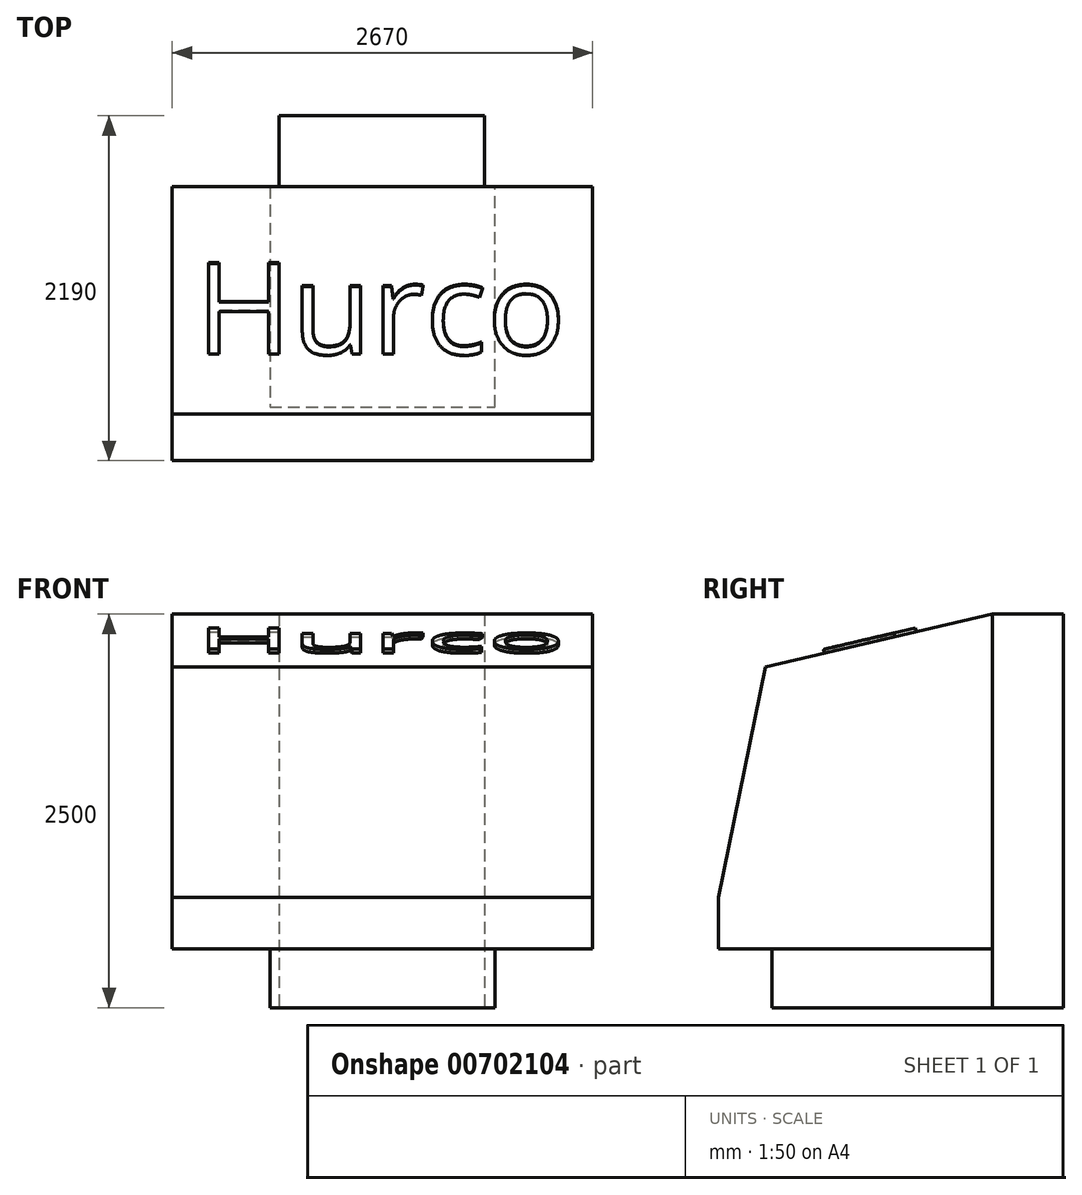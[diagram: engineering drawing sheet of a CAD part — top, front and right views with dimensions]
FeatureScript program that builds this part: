
annotation { "Feature Type Name" : "Feature", "Feature Type Description" : "" }
export const myFeature = defineFeature(function(context is Context, id is Id, definition is map)
    precondition{}
    {
        {
            var Q0;
            Q0=qCreatedBy(makeId("Top.planeOp"),FACE);
            var sketch = newSketch(context, id + "F0", { "sketchPlane" : qUnion([Q0])});
            skLineSegment(sketch, "E0.bottom", {"start": v(0, 0) * mm, "end": v(2670, 0) * mm});
            skLineSegment(sketch, "E0.top", {"start": v(0, 1740) * mm, "end": v(680, 1740) * mm});
            skLineSegment(sketch, "E0.left", {"start": v(0, 0) * mm, "end": v(0, 1740) * mm});
            skLineSegment(sketch, "E0.right", {"start": v(2670, 0) * mm, "end": v(2670, 1740) * mm});
            skLineSegment(sketch, "E1.top", {"start": v(680, 2190) * mm, "end": v(1985, 2190) * mm});
            skLineSegment(sketch, "E1.left", {"start": v(680, 1740) * mm, "end": v(680, 2190) * mm});
            skLineSegment(sketch, "E1.right", {"start": v(1985, 1740) * mm, "end": v(1985, 2190) * mm});
            skLineSegment(sketch, "E2.trimOffspring", {"start": v(1985, 1740) * mm, "end": v(2670, 1740) * mm});
            skSolve(sketch);
        }
        {
            var Q0;
            Q0=makeQuery(id+"F0.imprint","IMPRINT",FACE,{"disambiguationData":[TD([[makeQuery(id+"F0.imprint","IMPRINT",EDGE,{"derivedFrom":sQuery(id+"F0.wireOp",EDGE,"E0.bottom")}),1.0]])]});
            extrude(context, id + "F1", {"entities" : qUnion([Q0]), "depth" : 2500 * mm, "offsetDistance" : 25 * mm});
        }
        {
            var Q0;
            Q0=makeQuery(id+"F1.opExtrude","SWEPT_FACE",FACE,{"disambiguationData":[OSD([sQuery(id+"F0.wireOp",EDGE,"E0.right")])]});
            var sketch = newSketch(context, id + "F2", { "sketchPlane" : qUnion([Q0])});
            skLineSegment(sketch, "E3", {"start": v(0, 700) * mm, "end": v(296.46, 2163.72) * mm});
            skLineSegment(sketch, "E4", {"start": v(296.46, 2163.72) * mm, "end": v(1740, 2500) * mm});
            skLineSegment(sketch, "E5", {"start": v(1740, 2500) * mm, "end": v(0, 2500) * mm});
            skLineSegment(sketch, "E6", {"start": v(0, 2500) * mm, "end": v(0, 700) * mm});
            skSolve(sketch);
        }
        {
            var Q0;
            Q0=makeQuery(id+"F2.imprint","IMPRINT",FACE,{"disambiguationData":[TD([[makeQuery(id+"F2.imprint","IMPRINT",EDGE,{"derivedFrom":sQuery(id+"F2.wireOp",EDGE,"E3")}),1.0]])]});
            extrude(context, id + "F3", {"entities" : qUnion([Q0]), "operationType" : NewBodyOperationType.REMOVE, "endBound" : BoundingType.THROUGH_ALL, "oppositeDirection" : true, "depth" : 25 * mm, "offsetDistance" : 25 * mm});
        }
        {
            var Q0;
            Q0=makeQuery(id+"F3.boolean.opBoolean","COPY",FACE,{"derivedFrom":makeQuery(id+"F3.opExtrude","SWEPT_FACE",FACE,{"disambiguationData":[OSD([sQuery(id+"F2.wireOp",EDGE,"E4")])]})});
            var sketch = newSketch(context, id + "F4", { "sketchPlane" : qUnion([Q0])});
            skText(sketch, "E7", { "text": "Hurco", "fontName": "OpenSans-Regular.ttf"});
            const initialGuessF4  = {"E7": [0.14938, 1.17443, 1, 0, 0.5957]};
            skSetInitialGuess(sketch, initialGuessF4);
            skSolve(sketch);
        }
        {
            var Q0;
            Q0 = qSketchRegion(id + "F4", true);
            extrude(context, id + "F5", {"entities" : qUnion([Q0]), "operationType" : NewBodyOperationType.ADD, "depth" : 25 * mm, "offsetDistance" : 25 * mm});
        }
        {
            var Q0;
            Q0=makeQuery(id+"F1.opExtrude","CAP_FACE",FACE,{"disambiguationData":[OSD([sQuery(id+"F0.wireOp",EDGE,"E0.bottom"),sQuery(id+"F0.wireOp",EDGE,"E0.top"),sQuery(id+"F0.wireOp",EDGE,"E0.left"),sQuery(id+"F0.wireOp",EDGE,"E0.right"),sQuery(id+"F0.wireOp",EDGE,"E1.top"),sQuery(id+"F0.wireOp",EDGE,"E1.left"),sQuery(id+"F0.wireOp",EDGE,"E1.right"),sQuery(id+"F0.wireOp",EDGE,"E2.trimOffspring")])],"isStart":true});
            var sketch = newSketch(context, id + "F6", { "sketchPlane" : qUnion([Q0])});
            skLineSegment(sketch, "E8", {"start": v(0, -1740) * mm, "end": v(620, -1740) * mm});
            skLineSegment(sketch, "E9", {"start": v(620, -1740) * mm, "end": v(620, -340) * mm});
            skLineSegment(sketch, "E10", {"start": v(620, -340) * mm, "end": v(2050, -340) * mm});
            skLineSegment(sketch, "E11", {"start": v(2050, -340) * mm, "end": v(2050, -1740) * mm});
            skLineSegment(sketch, "E12", {"start": v(2050, -1740) * mm, "end": v(2670, -1740) * mm});
            skLineSegment(sketch, "E13", {"start": v(2670, -1740) * mm, "end": v(2670, 0) * mm});
            skLineSegment(sketch, "E14", {"start": v(2670, 0) * mm, "end": v(0, 0) * mm});
            skLineSegment(sketch, "E15", {"start": v(0, 0) * mm, "end": v(0, -1740) * mm});
            skSolve(sketch);
        }
        {
            var Q0;
            Q0=makeQuery(id+"F6.imprint","IMPRINT",FACE,{"disambiguationData":[TD([[makeQuery(id+"F6.imprint","IMPRINT",EDGE,{"derivedFrom":sQuery(id+"F6.wireOp",EDGE,"E8")}),1.0]])]});
            extrude(context, id + "F7", {"entities" : qUnion([Q0]), "operationType" : NewBodyOperationType.REMOVE, "oppositeDirection" : true, "depth" : 375 * mm, "offsetDistance" : 25 * mm});
        }
    });
